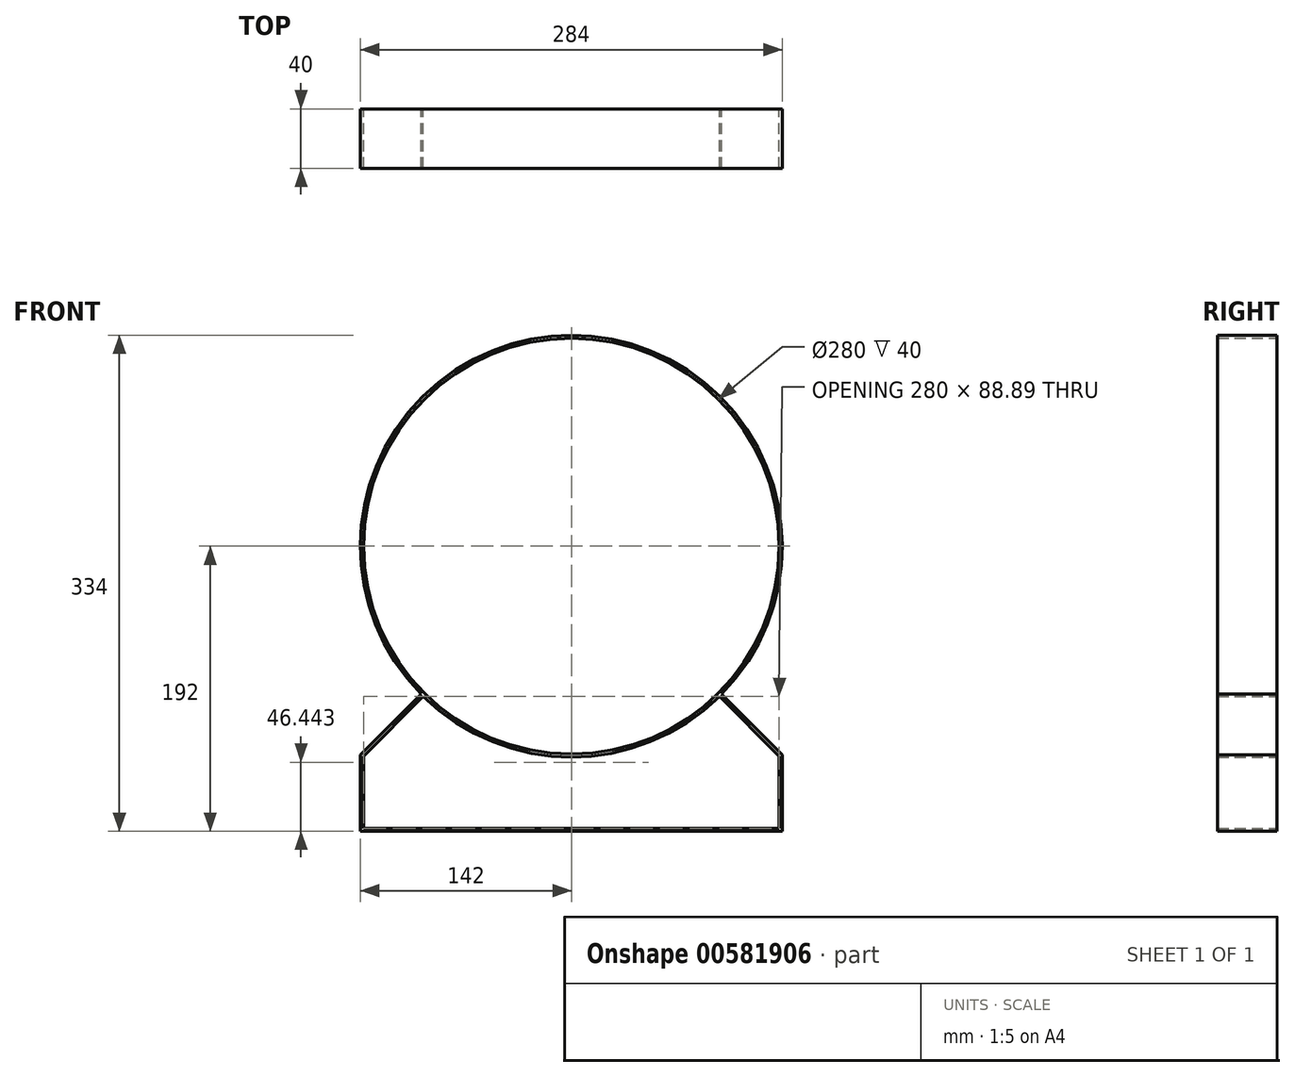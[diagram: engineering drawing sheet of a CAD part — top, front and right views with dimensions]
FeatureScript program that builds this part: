
annotation { "Feature Type Name" : "Feature", "Feature Type Description" : "" }
export const myFeature = defineFeature(function(context is Context, id is Id, definition is map)
    precondition{}
    {
        {
            var Q0;
            Q0=qCreatedBy(makeId("Front.planeOp"),FACE);
            var sketch = newSketch(context, id + "F0", { "sketchPlane" : qUnion([Q0])});
            skLineSegment(sketch, "E0", {"start": v(0, 0) * mm, "end": v(-679.96, 0) * mm, "construction": true});
            skLineSegment(sketch, "E1", {"start": v(0, 0) * mm, "end": v(0, 658.78) * mm, "construction": true});
            skLineSegment(sketch, "E2", {"start": v(0, 0) * mm, "end": v(-291.77, -291.77) * mm, "construction": true});
            skLineSegment(sketch, "E3", {"start": v(0, 0) * mm, "end": v(291.77, -291.77) * mm, "construction": true});
            skCircle(sketch, "E4", {"center": v(0, 0) * mm, "radius": 140 * mm});
            skCircle(sketch, "E5", {"center": v(0, 0) * mm, "radius": 142 * mm});
            skLineSegment(sketch, "E6", {"start": v(-142, -192) * mm, "end": v(0, -192) * mm});
            skLineSegment(sketch, "E7", {"start": v(-140, -190) * mm, "end": v(0, -190) * mm});
            skLineSegment(sketch, "E8", {"start": v(0, 0) * mm, "end": v(0, -311.11) * mm, "construction": true});
            skLineSegment(sketch, "E9", {"start": v(-140, -190) * mm, "end": v(-140, -141.41) * mm});
            skLineSegment(sketch, "E10", {"start": v(-142, -192) * mm, "end": v(-142, -140.59) * mm});
            skLineSegment(sketch, "E11", {"start": v(-101.11, -99.7) * mm, "end": v(-142, -140.59) * mm});
            skLineSegment(sketch, "E12", {"start": v(-99.7, -101.11) * mm, "end": v(-140, -141.41) * mm});
            skLineSegment(sketch, "E13.MirrorCS", {"start": v(99.7, -101.11) * mm, "end": v(140, -141.41) * mm});
            skLineSegment(sketch, "E14.MirrorCS", {"start": v(142, -192) * mm, "end": v(0, -192) * mm});
            skLineSegment(sketch, "E15.MirrorCS", {"start": v(140, -190) * mm, "end": v(0, -190) * mm});
            skLineSegment(sketch, "E16.MirrorCS", {"start": v(101.11, -99.7) * mm, "end": v(142, -140.59) * mm});
            skLineSegment(sketch, "E17.MirrorCS", {"start": v(140, -190) * mm, "end": v(140, -141.41) * mm});
            skLineSegment(sketch, "E18.MirrorCS", {"start": v(142, -192) * mm, "end": v(142, -140.59) * mm});
            skSolve(sketch);
        }
        {
            var Q0;
            Q0=qSketchRegion(id+"F0",true);
            extrude(context, id + "F1", {"entities" : qUnion([Q0]), "offsetDistance" : 25 * mm, "depth" : 40 * mm});
        }
    });
